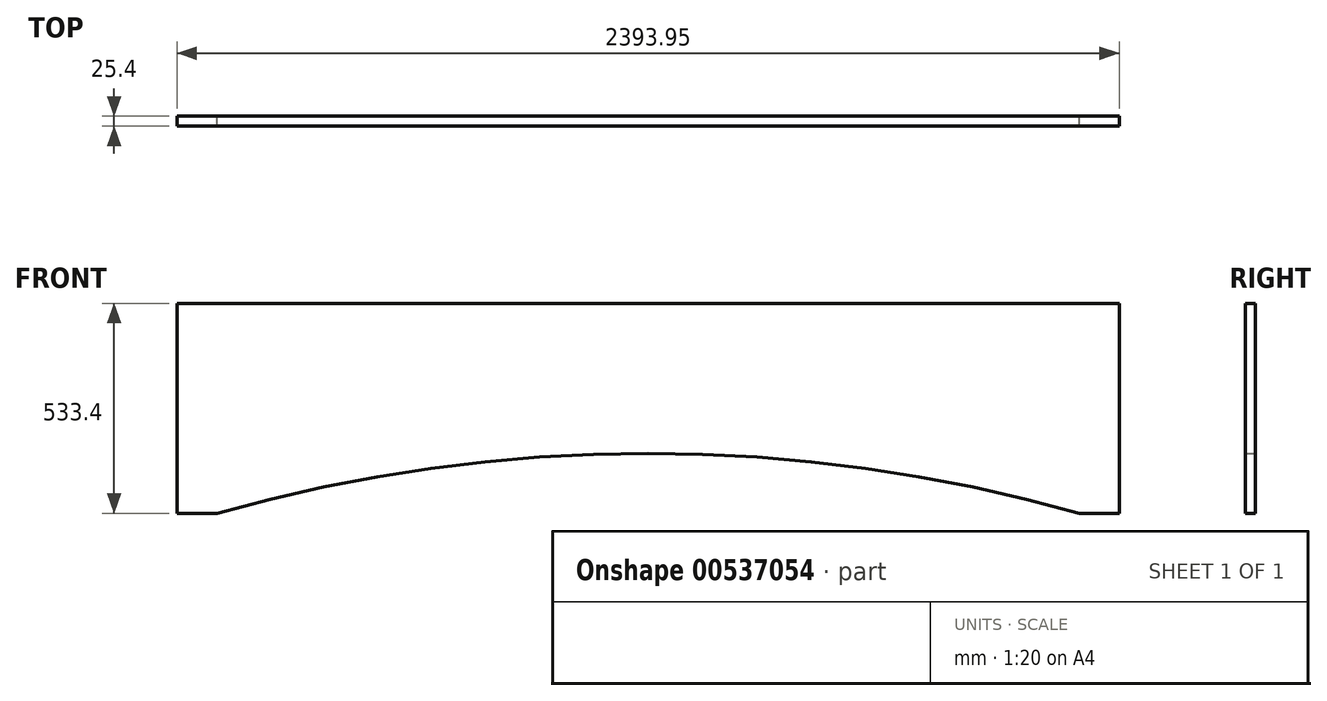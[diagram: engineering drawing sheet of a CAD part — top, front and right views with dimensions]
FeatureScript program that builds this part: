
annotation { "Feature Type Name" : "Feature", "Feature Type Description" : "" }
export const myFeature = defineFeature(function(context is Context, id is Id, definition is map)
    precondition{}
    {
        {
            var Q0;
            Q0=qCreatedBy(makeId("Front.planeOp"),FACE);
            var sketch = newSketch(context, id + "F0", { "sketchPlane" : qUnion([Q0])});
            skLineSegment(sketch, "E0", {"start": v(-94.2, 212.2) * mm, "end": v(2299.75, 212.2) * mm});
            skLineSegment(sketch, "E1", {"start": v(2299.75, 212.2) * mm, "end": v(2299.75, -321.2) * mm});
            skLineSegment(sketch, "E2", {"start": v(2299.75, -321.2) * mm, "end": v(2198.15, -321.2) * mm});
            skLineSegment(sketch, "E3", {"start": v(-94.2, 212.2) * mm, "end": v(-94.2, -321.2) * mm});
            skLineSegment(sketch, "E4", {"start": v(-94.2, -321.2) * mm, "end": v(7.4, -321.2) * mm});
            skArc(sketch, "E5", {"start": v(2198.15, -321.2) * mm, "mid": v(1102.77, -168.8) * mm, "end": v(7.4, -321.2) * mm});
            skPoint(sketch, "E6.start.orphan", {"position": v(1102.77, 212.2) * mm});
            skSolve(sketch);
        }
        {
            var Q0;
            Q0 = qSketchRegion(id + "F0", true);
            extrude(context, id + "F1", {"entities" : qUnion([Q0]), "depth" : 25.4 * mm, "offsetDistance" : 25.4 * mm});
        }
    });
